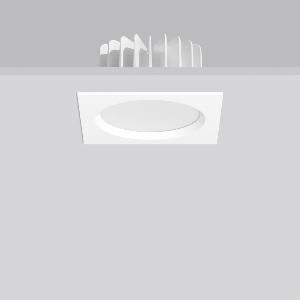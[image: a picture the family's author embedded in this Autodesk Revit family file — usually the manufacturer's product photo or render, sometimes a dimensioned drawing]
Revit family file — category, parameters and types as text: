
# Revit family: ledona_eco_square_901438_002_8ffa
name_source: partatom
category: Lighting Fixtures
units: mm (PartAtom-declared; Revit-internal decimal feet)

## family parameters
Cut with Voids When Loaded = No
Host = Face
Light Source = No
Part Type = Normal
Room Calculation Point = No
Round Connector Dimension = Use Diameter
Shared = No

## types (1)
- LEDONA ECO square (1 x LED Modul 830, 1500 lm, 3000)
    Apparent Load = 20 VA
    CIE Flux Codes = 49 81 97 100 100
    Color Rendering = 80
    Color Temperature = 3000
    Default Elevation = 1800 mm
    Height = 0 mm  [stored 0 ft]
    Lamp = 1 x LED Modul 830
    Lamp Light Flux = 1500 lm
    Lamp count = 1
    Length = 170 mm  [stored 0.557743 ft]
    Lifetime = 50000 h
    Luminous efficacy = 75 lm/W
    Manufacturer = RZB
    ModVariant = No
    Model = 901438.002
    Mounting Place = Ceiling
    Mounting Type = Recessed
    Number of Poles = 1
    OnlyDefault = Yes
    Power Factor = 1
    Product Name = LEDONA ECO square
    Product group = Recessed downlights
    ProductGroupID = 402
    Protection Class = Protection class I
    Protection Degree = IP 65
    RLX_Detail_Level = 1
    RLX_Emergency_Light_Flux = 0 lm
    RLX_Emergency_Type = 0
    RLX_Emergency_Type_DB = No
    RlxData = <blob elided: 31345 chars, md5=50dfdfff>
    Socket = socket
    Standby Power = 0 W
    System Light Flux = 1500 lm
    System Power = 20 W
    Type Comments = Product without accessories
    Type Image = 901438.002.jpg
    URL = http://relux.com
    VarID = ---
    Voltage = 230 V
    Voltage Range = 220-240 V
    Weight = 0.00 kg
    Width = 170 mm  [stored 0.557743 ft]

note: [stored X ft] marks values corroborated as IEEE doubles in the binary element streams (Revit-internal decimal feet)

## geometry (parser evidence)
native form markers: Blend x4, Sweep x11
no freeform markers — native parametric forms only
